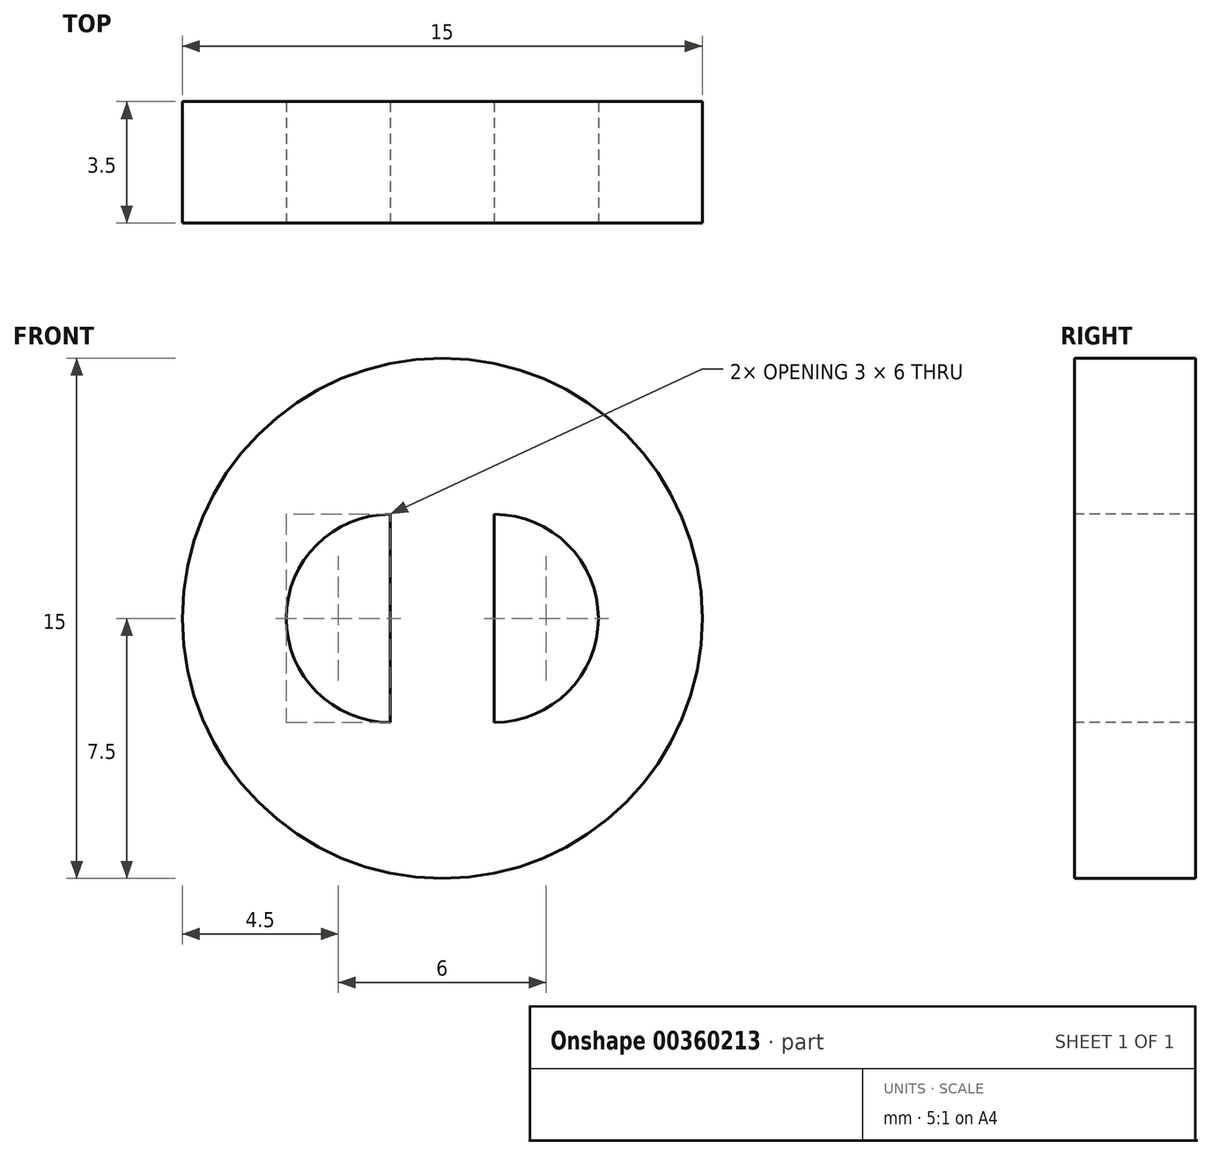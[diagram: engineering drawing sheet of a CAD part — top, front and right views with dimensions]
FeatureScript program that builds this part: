
annotation { "Feature Type Name" : "Feature", "Feature Type Description" : "" }
export const myFeature = defineFeature(function(context is Context, id is Id, definition is map)
    precondition{}
    {
        {
            var Q0;
            Q0=qCreatedBy(makeId("Front.planeOp"),FACE);
            var sketch = newSketch(context, id + "F0", { "sketchPlane" : qUnion([Q0])});
            skCircle(sketch, "E0", {"center": v(0, 0) * mm, "radius": 7.5 * mm});
            skSolve(sketch);
        }
        {
            var Q0;
            Q0=makeQuery(id+"F0.imprint","IMPRINT",FACE,{"disambiguationData":[TD([[makeQuery(id+"F0.imprint","IMPRINT",EDGE,{"derivedFrom":sQuery(id+"F0.wireOp",EDGE,"E0")}),1.0]])]});
            extrude(context, id + "F1", {"entities" : qUnion([Q0]), "depth" : 3.5 * mm});
        }
        {
            var Q0;
            Q0=makeQuery(id+"F1.opExtrude","CAP_FACE",FACE,{"disambiguationData":[OSD([sQuery(id+"F0.wireOp",EDGE,"E0")])],"isStart":false});
            var sketch = newSketch(context, id + "F2", { "sketchPlane" : qUnion([Q0])});
            skLineSegment(sketch, "E1", {"start": v(0, 0) * mm, "end": v(0, 3) * mm});
            skLineSegment(sketch, "E2", {"start": v(0, 3) * mm, "end": v(0, -3) * mm});
            skLineSegment(sketch, "E3", {"start": v(0, -3) * mm, "end": v(-1.5, -3) * mm});
            skLineSegment(sketch, "E4", {"start": v(-1.5, -3) * mm, "end": v(1.5, -3) * mm});
            skLineSegment(sketch, "E5", {"start": v(1.5, -3) * mm, "end": v(1.5, 3) * mm});
            skLineSegment(sketch, "E6", {"start": v(1.5, 3) * mm, "end": v(-1.5, 3) * mm});
            skLineSegment(sketch, "E7", {"start": v(-1.5, 3) * mm, "end": v(-1.5, -3) * mm});
            skArc(sketch, "E8", {"start": v(-1.5, 3) * mm, "mid": v(-4.5, 0) * mm, "end": v(-1.5, -3) * mm});
            skArc(sketch, "E9", {"start": v(1.5, -3) * mm, "mid": v(4.5, 0) * mm, "end": v(1.5, 3) * mm});
            skSolve(sketch);
        }
        {
            var Q0;
            Q0=makeQuery(id+"F2.imprint","IMPRINT",FACE,{"disambiguationData":[TD([[makeQuery(id+"F2.imprint","IMPRINT",EDGE,{"derivedFrom":sQuery(id+"F2.wireOp",EDGE,"E5")}),-1.0]])]});
            var Q1;
            Q1=makeQuery(id+"F2.imprint","IMPRINT",FACE,{"disambiguationData":[TD([[makeQuery(id+"F2.imprint","IMPRINT",EDGE,{"derivedFrom":sQuery(id+"F2.wireOp",EDGE,"E7")}),-1.0]])]});
            extrude(context, id + "F3", {"entities" : qUnion([Q0, Q1]), "operationType" : NewBodyOperationType.REMOVE, "oppositeDirection" : true, "depth" : 25 * mm});
        }
    });
